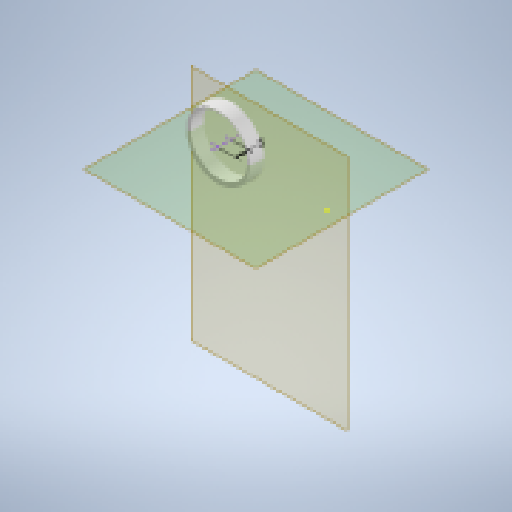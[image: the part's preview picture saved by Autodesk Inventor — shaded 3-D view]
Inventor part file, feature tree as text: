
AUTODESK INVENTOR PART (.ipt)
format: ipt  version: 2023 (Build 270158000, 158)  size: 319,488 bytes
history: native  units: mm
features: other x12, sketch x9, extrude x3, projected_geometry x2, loft x1
ambient origin geometry x8: Origin, YZ Plane, XZ Plane, XY Plane, X Axis, Y Axis, Z Axis, Center Point
bodies: Body1 (feature_tree)
feature tree (27):
  sketch  "Esquisse1"
  other  "Plan de construction2"
  sketch  "Esquisse2"
  other  "Plan de construction4"
  sketch  "Esquisse3"
  other  "Plan de construction5"
  loft  "Lissage2"
  extrude  "Extrusion2"  Depth=0.5mm
  other  "Plan de construction6"
  sketch  "Esquisse6"
  sketch  "Esquisse7"
  sketch  "Esquisse8"
  other  "Révolution1"
  extrude  "Extrusion3"  Depth=2.0mm
  extrude  "Extrusion4"  Depth=1.0mm
  other  "Référence1"
  other  "Plan de construction1"
  other  "Plan de construction3"
  other  "Référence2"
  sketch  "Esquisse5"
  projected_geometry  "Boucle projetée1"
  sketch  "Esquisse9"
  projected_geometry  "Boucle projetée2"
  sketch  "Esquisse10"
  other  "<userpath>\Desktop\PE-SM\3D\Ensemble.iam"
  other  "Ensemble.iam"
  other  "PE:1"
